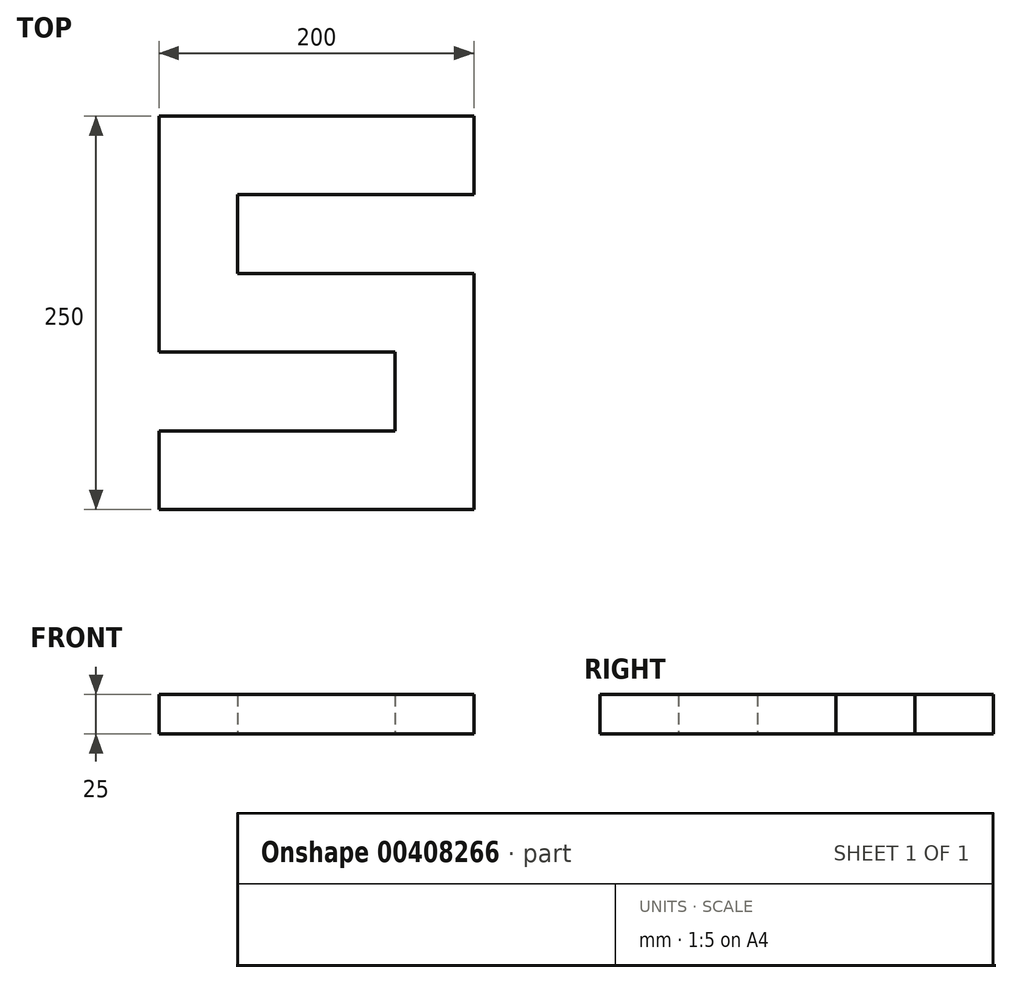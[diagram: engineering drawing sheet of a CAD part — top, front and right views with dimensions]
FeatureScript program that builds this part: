
annotation { "Feature Type Name" : "Feature", "Feature Type Description" : "" }
export const myFeature = defineFeature(function(context is Context, id is Id, definition is map)
    precondition{}
    {
        {
            var Q0;
            Q0=qCreatedBy(makeId("Top.planeOp"),FACE);
            var sketch = newSketch(context, id + "F0", { "sketchPlane" : qUnion([Q0])});
            skLineSegment(sketch, "E0.bottom", {"start": v(101.64, 150) * mm, "end": v(-98.36, 150) * mm});
            skLineSegment(sketch, "E0.top", {"start": v(101.64, 100) * mm, "end": v(-98.36, 100) * mm});
            skLineSegment(sketch, "E0.left", {"start": v(101.64, 150) * mm, "end": v(101.64, 100) * mm});
            skLineSegment(sketch, "E0.right", {"start": v(-98.36, 150) * mm, "end": v(-98.36, 100) * mm});
            skLineSegment(sketch, "E1.bottom", {"start": v(-98.36, 150) * mm, "end": v(-48.36, 150) * mm});
            skLineSegment(sketch, "E1.top", {"start": v(-98.36, 0) * mm, "end": v(-48.36, 0) * mm});
            skLineSegment(sketch, "E1.left", {"start": v(-98.36, 150) * mm, "end": v(-98.36, 0) * mm});
            skLineSegment(sketch, "E1.right", {"start": v(-48.36, 150) * mm, "end": v(-48.36, 0) * mm});
            skLineSegment(sketch, "E2.bottom", {"start": v(-98.36, 0) * mm, "end": v(101.64, 0) * mm});
            skLineSegment(sketch, "E2.top", {"start": v(-98.36, 50) * mm, "end": v(101.64, 50) * mm});
            skLineSegment(sketch, "E2.left", {"start": v(-98.36, 0) * mm, "end": v(-98.36, 50) * mm});
            skLineSegment(sketch, "E2.right", {"start": v(101.64, 0) * mm, "end": v(101.64, 50) * mm});
            skLineSegment(sketch, "E3.bottom", {"start": v(101.64, 50) * mm, "end": v(51.64, 50) * mm});
            skLineSegment(sketch, "E3.top", {"start": v(101.64, -100) * mm, "end": v(51.64, -100) * mm});
            skLineSegment(sketch, "E3.left", {"start": v(101.64, 50) * mm, "end": v(101.64, -100) * mm});
            skLineSegment(sketch, "E3.right", {"start": v(51.64, 50) * mm, "end": v(51.64, -100) * mm});
            skLineSegment(sketch, "E4.bottom", {"start": v(101.64, -100) * mm, "end": v(-98.36, -100) * mm});
            skLineSegment(sketch, "E4.top", {"start": v(101.64, -50) * mm, "end": v(-98.36, -50) * mm});
            skLineSegment(sketch, "E4.left", {"start": v(101.64, -100) * mm, "end": v(101.64, -50) * mm});
            skLineSegment(sketch, "E4.right", {"start": v(-98.36, -100) * mm, "end": v(-98.36, -50) * mm});
            skSolve(sketch);
        }
        {
            var Q0;
            Q0 = qSketchRegion(id + "F0", true);
            extrude(context, id + "F1", {"entities" : qUnion([Q0]), "depth" : 25 * mm});
        }
    });
